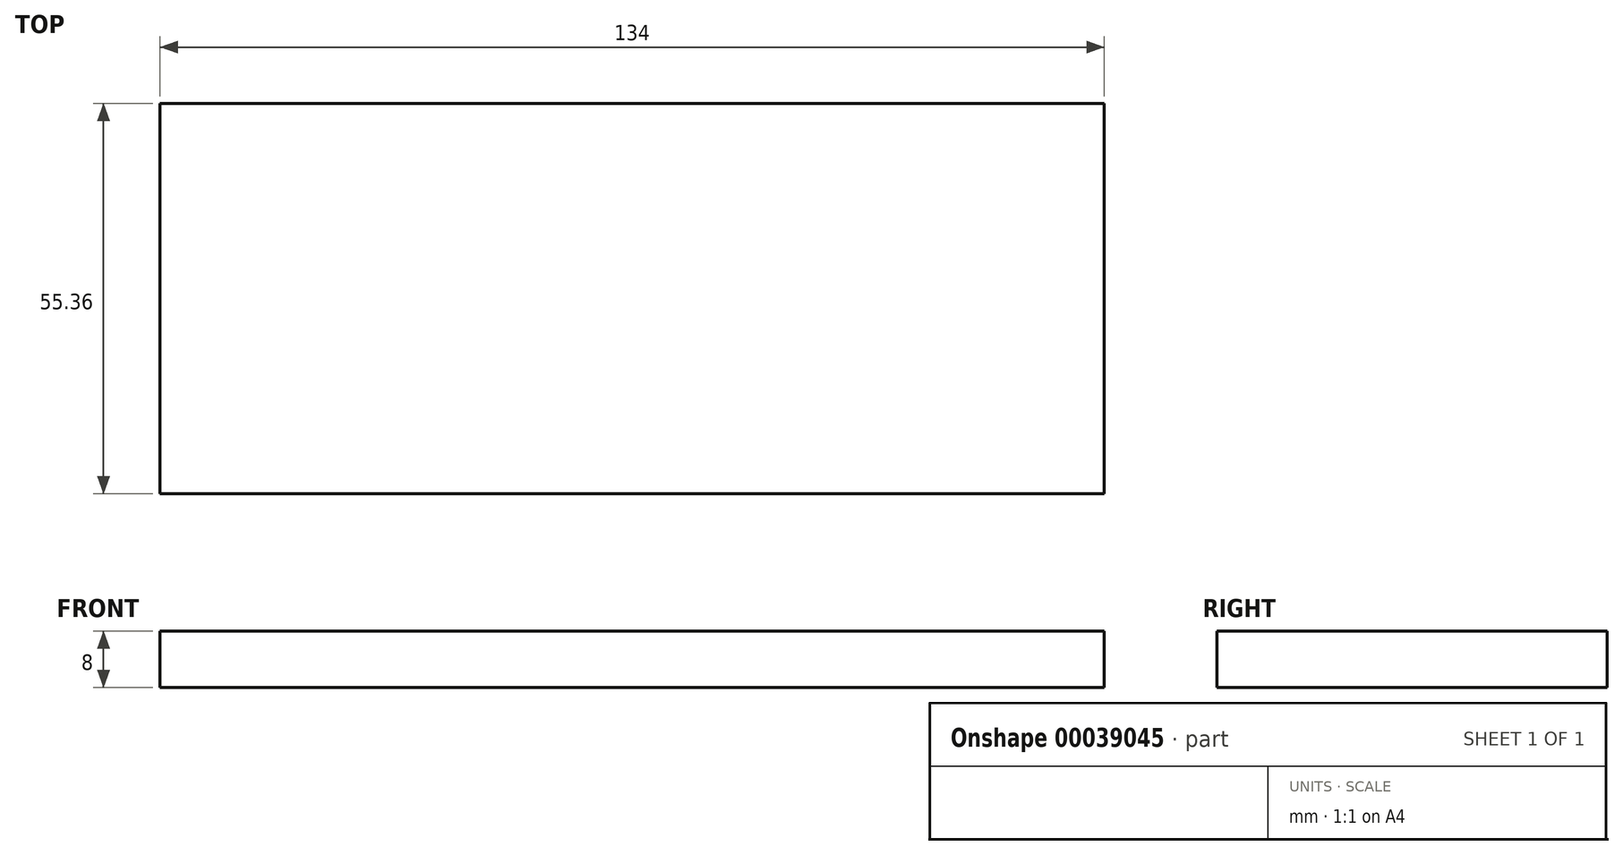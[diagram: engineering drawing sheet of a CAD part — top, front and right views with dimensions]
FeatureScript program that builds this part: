
annotation { "Feature Type Name" : "Feature", "Feature Type Description" : "" }
export const myFeature = defineFeature(function(context is Context, id is Id, definition is map)
    precondition{}
    {
        {
            var Q0;
            Q0=qCreatedBy(makeId("Right.planeOp"),FACE);
            var sketch = newSketch(context, id + "F0", { "sketchPlane" : qUnion([Q0])});
            skLineSegment(sketch, "E0.0", {"start": v(-27.68, 4) * mm, "end": v(27.68, 4) * mm});
            skLineSegment(sketch, "E1", {"start": v(-27.68, 4) * mm, "end": v(-27.68, -4) * mm});
            skLineSegment(sketch, "E2", {"start": v(-27.68, -4) * mm, "end": v(27.68, -4) * mm});
            skLineSegment(sketch, "E3", {"start": v(27.68, -4) * mm, "end": v(27.68, 4) * mm});
            skSolve(sketch);
        }
        {
            var Q0;
            Q0=makeQuery(id+"F0.imprint","IMPRINT",FACE,{"disambiguationData":[TD([[makeQuery(id+"F0.imprint","IMPRINT",EDGE,{"derivedFrom":sQuery(id+"F0.wireOp",EDGE,"E0.0")}),-1.0]])]});
            extrude(context, id + "F1", {"entities" : qUnion([Q0]), "depth" : (150 - 16) * mm});
        }
    });
